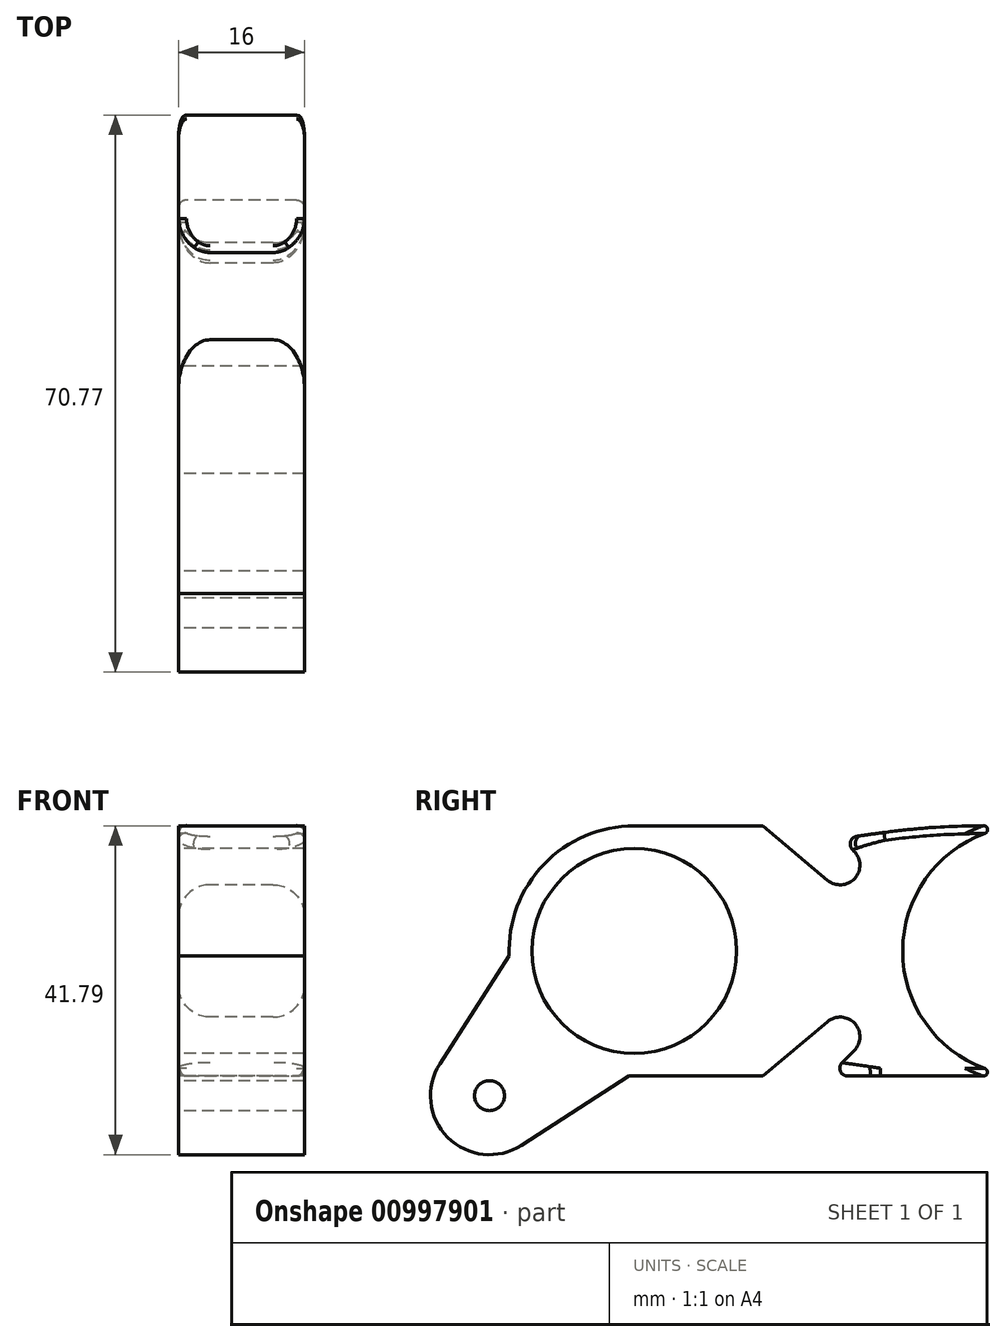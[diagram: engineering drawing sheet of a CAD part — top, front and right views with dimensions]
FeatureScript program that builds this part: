
annotation { "Feature Type Name" : "Feature", "Feature Type Description" : "" }
export const myFeature = defineFeature(function(context is Context, id is Id, definition is map)
    precondition{}
    {
        {
            var Q0;
            Q0=qCreatedBy(makeId("Right.planeOp"),FACE);
            var sketch = newSketch(context, id + "F0", { "sketchPlane" : qUnion([Q0])});
            skCircle(sketch, "E0", {"center": v(-68.38, -18.38) * mm, "radius": 1.9 * mm});
            skLineSegment(sketch, "E1", {"start": v(-50, 0) * mm, "end": v(-68.38, -18.38) * mm, "construction": true});
            skCircle(sketch, "E2", {"center": v(-50, 0) * mm, "radius": 15.9 * mm});
            skLineSegment(sketch, "E3", {"start": v(-50, 0) * mm, "end": v(-50, 15.9) * mm, "construction": true});
            skCircle(sketch, "E4", {"center": v(-50, 0) * mm, "radius": 13 * mm});
            skLineSegment(sketch, "E5", {"start": v(-50, 15.9) * mm, "end": v(-23.83, 15.9) * mm});
            skLineSegment(sketch, "E6", {"start": v(-50, -15.9) * mm, "end": v(0, -15.9) * mm});
            skArc(sketch, "E7", {"start": v(0, 15.9) * mm, "mid": v(-15.9, 0) * mm, "end": v(0, -15.9) * mm});
            skLineSegment(sketch, "E8", {"start": v(-50, 0) * mm, "end": v(0, 0) * mm, "construction": true});
            skLineSegment(sketch, "E9", {"start": v(0, 15.9) * mm, "end": v(0, -15.9) * mm});
            skCircle(sketch, "E10", {"center": v(-23.83, 10.9) * mm, "radius": 2.5 * mm});
            skCircle(sketch, "E11", {"center": v(-23.83, 10.9) * mm, "radius": 4 * mm, "construction": true});
            skLineSegment(sketch, "E12", {"start": v(-23.83, 10.9) * mm, "end": v(-23.83, 15.9) * mm, "construction": true});
            skLineSegment(sketch, "E13", {"start": v(-23.83, 10.9) * mm, "end": v(-28.83, 15.9) * mm});
            skLineSegment(sketch, "E14", {"start": v(-23.83, 10.9) * mm, "end": v(-22.06, 12.67) * mm, "construction": true});
            skLineSegment(sketch, "E15", {"start": v(-22.06, 12.67) * mm, "end": v(-25.3, 15.9) * mm});
            skLineSegment(sketch, "E16", {"start": v(-23.83, 10.9) * mm, "end": v(-25.44, 8.99) * mm});
            skLineSegment(sketch, "E17", {"start": v(-25.44, 8.99) * mm, "end": v(-33.65, 15.9) * mm});
            skLineSegment(sketch, "E18.MirrorCS", {"start": v(-23.83, -10.9) * mm, "end": v(-25.44, -8.99) * mm});
            skCircle(sketch, "E19.MirrorC", {"center": v(-23.83, -10.9) * mm, "radius": 4 * mm, "construction": true});
            skLineSegment(sketch, "E20.MirrorCS", {"start": v(-25.44, -8.99) * mm, "end": v(-33.65, -15.9) * mm});
            skCircle(sketch, "E21.MirrorC", {"center": v(-23.83, -10.9) * mm, "radius": 2.5 * mm});
            skLineSegment(sketch, "E22.MirrorCS", {"start": v(-23.83, -10.9) * mm, "end": v(-22.06, -12.67) * mm, "construction": true});
            skLineSegment(sketch, "E23.MirrorCS", {"start": v(-23.83, -10.9) * mm, "end": v(-23.83, -15.9) * mm, "construction": true});
            skLineSegment(sketch, "E24.MirrorCS", {"start": v(-23.83, -10.9) * mm, "end": v(-28.83, -15.9) * mm});
            skLineSegment(sketch, "E25.MirrorCS", {"start": v(-22.06, -12.67) * mm, "end": v(-25.3, -15.9) * mm});
            skCircle(sketch, "E26.converted", {"center": v(-68.38, -18.38) * mm, "radius": 7.5 * mm});
            skLineSegment(sketch, "E27", {"start": v(-50, 0) * mm, "end": v(-40.8, -9.2) * mm});
            skLineSegment(sketch, "E28", {"start": v(-50, 0) * mm, "end": v(-59.2, 9.2) * mm});
            skLineSegment(sketch, "E29", {"start": v(-64.32, -24.69) * mm, "end": v(-42.96, -10.93) * mm});
            skLineSegment(sketch, "E30", {"start": v(-74.69, -14.32) * mm, "end": v(-60.93, 7.04) * mm});
            skLineSegment(sketch, "E31", {"start": v(-61.24, -11.24) * mm, "end": v(-54.27, -18.21) * mm});
            skLineSegment(sketch, "E32", {"start": v(-61.24, -11.24) * mm, "end": v(-68.21, -4.27) * mm});
            skFitSpline(sketch, "E33", {"points": [v(-23.68, 14.28) * mm, v(-12.1, 15.68) * mm, v(0, 15.9) * mm], "startDerivative": vector(23.22, 3.42) * mm, "endDerivative": vector(24.14, -0.18) * mm});
            skSolve(sketch);
        }
        {
            var Q0;
            {var subQ0=sQuery(id+"F0.wireOp",EDGE,"E6");Q0=makeQuery(id+"F0.imprint","IMPRINT",FACE,{"disambiguationData":[TD([[makeQuery(id+"F0.imprint","IMPRINT",EDGE,{"derivedFrom":subQ0}),1.0]])]});}
            var Q1;
            Q1=makeQuery(id+"F0.imprint","IMPRINT",FACE,{"disambiguationData":[TD([[makeQuery(id+"F0.imprint","IMPRINT",EDGE,{"derivedFrom":sQuery(id+"F0.wireOp",EDGE,"E4")}),-1.0]])]});
            var Q2;
            {var subQ0=sQuery(id+"F0.wireOp",EDGE,"E30");var subQ1=sQuery(id+"F0.wireOp",EDGE,"E2");var subQ2=makeQuery(id+"F0.imprint","INTERSECT",VERTEX,{"derivedFrom":[subQ1,subQ0]});Q2=makeQuery(id+"F0.imprint","IMPRINT",FACE,{"disambiguationData":[TD([[makeQuery(id+"F0.imprint","IMPRINT",EDGE,{"disambiguationData":[TD([[subQ2,-1.0]])],"derivedFrom":subQ1}),1.0]])]});}
            var Q3;
            {var subQ0=sQuery(id+"F0.wireOp",EDGE,"3086c063-87a8-4bc6-9855-3dacc8c76d5f");Q3=makeQuery(id+"F0.imprint","IMPRINT",FACE,{"disambiguationData":[TD([[makeQuery(id+"F0.imprint","IMPRINT",EDGE,{"derivedFrom":subQ0}),-1.0]])]});}
            extrude(context, id + "F1", {"entities" : qUnion([Q0, Q1, Q2, Q3]), "endBound" : BoundingType.SYMMETRIC, "depth" : 16 * mm, "offsetDistance" : 25 * mm});
        }
        {
            var Q0;
            Q0=makeQuery(id+"F1.opExtrude","CAP_EDGE",EDGE,{"disambiguationData":[OSD([sQuery(id+"F0.wireOp",EDGE,"E10")])],"isStart":false});
            var Q1;
            Q1=makeQuery(id+"F1.opExtrude","CAP_EDGE",EDGE,{"disambiguationData":[OSD([sQuery(id+"F0.wireOp",EDGE,"E10")])],"isStart":true});
            var Q2;
            Q2=makeQuery(id+"F1.opExtrude","CAP_EDGE",EDGE,{"disambiguationData":[OSD([sQuery(id+"F0.wireOp",EDGE,"E21.MirrorC")])],"isStart":false});
            var Q3;
            Q3=makeQuery(id+"F1.opExtrude","CAP_EDGE",EDGE,{"disambiguationData":[OSD([sQuery(id+"F0.wireOp",EDGE,"E25.MirrorCS")])],"isStart":true});
            fillet(context, id + "F2", {"entities" : qUnion([Q0, Q1, Q2, Q3]), "tangentPropagation" : true, "radius" : 4 * mm, "defaultsChanged" : false, "vertexSettings" : [], "allowEdgeOverflow" : false});
        }
        {
            var Q0;
            {var subQ0=sQuery(id+"F0.wireOp",EDGE,"E17");var subQ1=sQuery(id+"F0.wireOp",EDGE,"E5");Q0=makeQuery(id+"FOFGYg2byATrX0D_1.opFillet","BLEND_EDGE",EDGE,{"blendedFrom":[makeQuery(id+"FRAa2dbH6Hqwcij_0.opExtrude","SWEPT_EDGE",EDGE,{"disambiguationData":[OSD([subQ1,subQ0])]}),makeQuery(id+"FRAa2dbH6Hqwcij_0.opExtrude","CAP_FACE",FACE,{"disambiguationData":[OSD([sQuery(id+"F0.wireOp",EDGE,"E0"),sQuery(id+"F0.wireOp",EDGE,"E2"),sQuery(id+"F0.wireOp",EDGE,"hsWxHISy-cXQM-S3Z0-jr71-N0sfxZjs8Wpq"),sQuery(id+"F0.wireOp",EDGE,"sPQkueuq-XMce-aMQn-24Dd-XQsdJudEM9Tt"),sQuery(id+"F0.wireOp",EDGE,"28696516-e2f3-41bc-ab6d-29d823c51189.trimOffspring"),sQuery(id+"F0.wireOp",EDGE,"E4"),subQ1,sQuery(id+"F0.wireOp",EDGE,"E6"),sQuery(id+"F0.wireOp",EDGE,"E7"),sQuery(id+"F0.wireOp",EDGE,"E10"),sQuery(id+"F0.wireOp",EDGE,"E15"),subQ0])],"isStart":true})],"blendedInto":[makeQuery(id+"FRAa2dbH6Hqwcij_0.opExtrude","CAP_FACE",FACE,{"disambiguationData":[OSD([sQuery(id+"F0.wireOp",EDGE,"E0"),sQuery(id+"F0.wireOp",EDGE,"E2"),sQuery(id+"F0.wireOp",EDGE,"hsWxHISy-cXQM-S3Z0-jr71-N0sfxZjs8Wpq"),sQuery(id+"F0.wireOp",EDGE,"sPQkueuq-XMce-aMQn-24Dd-XQsdJudEM9Tt"),sQuery(id+"F0.wireOp",EDGE,"28696516-e2f3-41bc-ab6d-29d823c51189.trimOffspring"),sQuery(id+"F0.wireOp",EDGE,"E4"),subQ1,sQuery(id+"F0.wireOp",EDGE,"E6"),sQuery(id+"F0.wireOp",EDGE,"E7"),sQuery(id+"F0.wireOp",EDGE,"E10"),sQuery(id+"F0.wireOp",EDGE,"E15"),subQ0])],"isStart":true})]});}
            var Q1;
            Q1=makeQuery(id+"FRAa2dbH6Hqwcij_0.opExtrude","CAP_EDGE",EDGE,{"disambiguationData":[OSD([sQuery(id+"F0.wireOp",EDGE,"E17")])],"isStart":true});
            var Q2;
            Q2=makeQuery(id+"FRAa2dbH6Hqwcij_0.opExtrude","CAP_EDGE",EDGE,{"disambiguationData":[OSD([sQuery(id+"F0.wireOp",EDGE,"E10")])],"isStart":true});
            var Q3;
            Q3=makeQuery(id+"FRAa2dbH6Hqwcij_0.opExtrude","CAP_EDGE",EDGE,{"disambiguationData":[OSD([sQuery(id+"F0.wireOp",EDGE,"E17")])],"isStart":true});
            var Q4;
            Q4=makeQuery(id+"F1.opExtrude","SWEPT_EDGE",EDGE,{"disambiguationData":[OSD([sQuery(id+"F0.wireOp",EDGE,"E5"),sQuery(id+"F0.wireOp",EDGE,"E7"),sQuery(id+"F0.wireOp",EDGE,"E9")])]});
            var Q5;
            Q5=makeQuery(id+"F1.opExtrude","SWEPT_EDGE",EDGE,{"disambiguationData":[OSD([sQuery(id+"F0.wireOp",EDGE,"E6"),sQuery(id+"F0.wireOp",EDGE,"E7"),sQuery(id+"F0.wireOp",EDGE,"E9")])]});
            fillet(context, id + "F3", {"entities" : qUnion([Q0, Q1, Q2, Q3, Q4, Q5]), "tangentPropagation" : true, "radius" : 0.5 * mm, "defaultsChanged" : false, "vertexSettings" : [], "allowEdgeOverflow" : false});
        }
        {
            var Q0;
            {var subQ0=sQuery(id+"F0.wireOp",EDGE,"E6");Q0=makeQuery(id+"F1.opExtrude","CAP_EDGE",EDGE,{"disambiguationData":[OSD([subQ0]),TDD([makeQuery(id+"F0.imprint","IMPRINT",EDGE,{"disambiguationData":[TD([[makeQuery(id+"F0.imprint","INTERSECT",VERTEX,{"derivedFrom":[subQ0,sQuery(id+"F0.wireOp",EDGE,"E25.MirrorCS")]}),-1.0]])],"derivedFrom":subQ0})])],"isStart":false});}
            fillet(context, id + "F4", {"entities" : qUnion([Q0]), "tangentPropagation" : true, "radius" : 1 * mm, "defaultsChanged" : true, "vertexSettings" : [], "allowEdgeOverflow" : false});
        }
        {
            var Q0;
            {var subQ2=sQuery(id+"F0.wireOp",EDGE,"E29");var subQ4=sQuery(id+"F0.wireOp",EDGE,"E4");var subQ5=makeQuery(id+"F0.imprint","INTERSECT",VERTEX,{"derivedFrom":[subQ4,subQ2]});Q0=makeQuery(id+"F0.imprint","IMPRINT",FACE,{"disambiguationData":[TD([[makeQuery(id+"F0.imprint","IMPRINT",EDGE,{"disambiguationData":[TD([[subQ5,1.0]])],"derivedFrom":subQ4}),-1.0]])]});}
            var Q1;
            {var subQ0=sQuery(id+"F0.wireOp",EDGE,"E32");Q1=makeQuery(id+"F0.imprint","IMPRINT",FACE,{"disambiguationData":[TD([[makeQuery(id+"F0.imprint","IMPRINT",EDGE,{"derivedFrom":subQ0}),-1.0]])]});}
            var Q2;
            {var subQ0=sQuery(id+"F0.wireOp",EDGE,"E31");Q2=makeQuery(id+"F0.imprint","IMPRINT",FACE,{"disambiguationData":[TD([[makeQuery(id+"F0.imprint","IMPRINT",EDGE,{"derivedFrom":subQ0}),1.0]])]});}
            var Q3;
            {var subQ0=sQuery(id+"F0.wireOp",EDGE,"E31");Q3=makeQuery(id+"F0.imprint","IMPRINT",FACE,{"disambiguationData":[TD([[makeQuery(id+"F0.imprint","IMPRINT",EDGE,{"derivedFrom":subQ0}),-1.0]])]});}
            var Q4;
            Q4=makeQuery(id+"F0.imprint","IMPRINT",FACE,{"disambiguationData":[TD([[makeQuery(id+"F0.imprint","IMPRINT",EDGE,{"derivedFrom":sQuery(id+"F0.wireOp",EDGE,"E0")}),-1.0]])]});
            extrude(context, id + "F5", {"entities" : qUnion([Q0, Q1, Q2, Q3, Q4]), "operationType" : NewBodyOperationType.ADD, "endBound" : BoundingType.SYMMETRIC, "depth" : 16 * mm, "offsetDistance" : 25 * mm});
        }
    });
